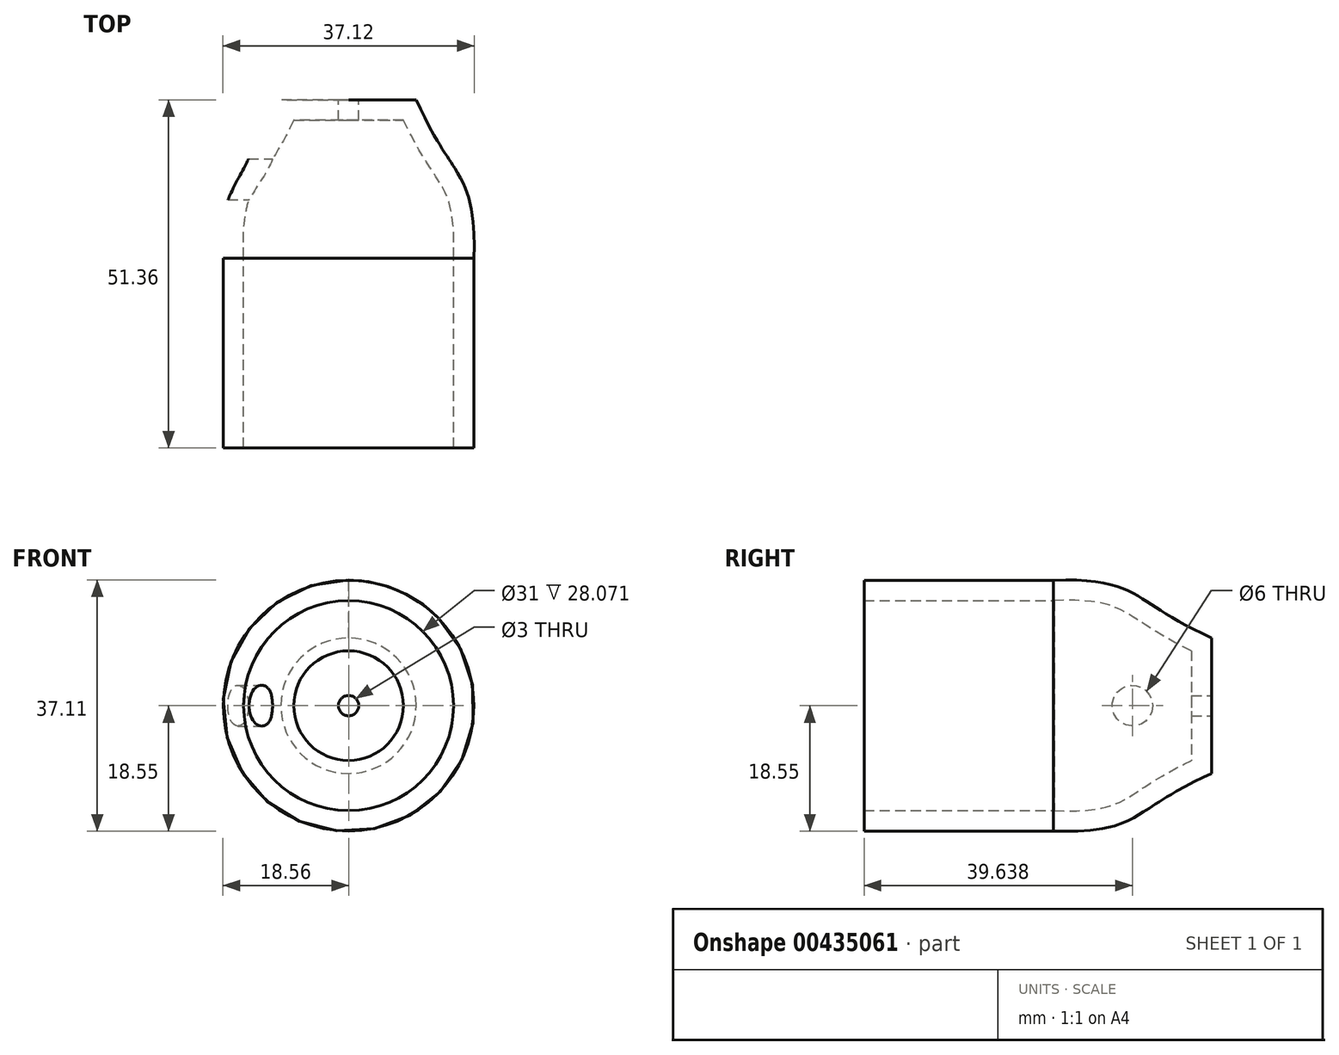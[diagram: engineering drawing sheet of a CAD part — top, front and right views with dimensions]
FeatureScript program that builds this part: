
annotation { "Feature Type Name" : "Feature", "Feature Type Description" : "" }
export const myFeature = defineFeature(function(context is Context, id is Id, definition is map)
    precondition{}
    {
        {
            var Q0;
            Q0=qCreatedBy(makeId("Front.planeOp"),FACE);
            var sketch = newSketch(context, id + "F0", { "sketchPlane" : qUnion([Q0])});
            skCircle(sketch, "E0", {"center": v(0, 0) * mm, "radius": 15.5 * mm});
            skCircle(sketch, "E1.0", {"center": v(0, 0) * mm, "radius": 18.5 * mm});
            skSolve(sketch);
        }
        {
            var Q0;
            Q0 = qSketchRegion(id + "F0", true);
            extrude(context, id + "F1", {"entities" : qUnion([Q0]), "depth" : 28 * mm});
        }
        {
            var Q0;
            Q0=qCreatedBy(makeId("Top.planeOp"),FACE);
            var sketch = newSketch(context, id + "F2", { "sketchPlane" : qUnion([Q0])});
            skLineSegment(sketch, "E2", {"start": v(0, 0) * mm, "end": v(-18.5, 0) * mm});
            skLineSegment(sketch, "E3", {"start": v(0, 23.36) * mm, "end": v(-10, 23.36) * mm});
            skFitSpline(sketch, "E4", {"points": [v(-10, 23.36) * mm, v(-15.86, 12.99) * mm, v(-18.5, 0) * mm], "startDerivative": vector(-16.01, -35.2) * mm, "endDerivative": vector(2.08, -43.63) * mm});
            skLineSegment(sketch, "E5", {"start": v(0, 23.36) * mm, "end": v(0, 0) * mm});
            skSolve(sketch);
        }
        {
            var Q0;
            Q0=makeQuery(id+"F2.imprint","IMPRINT",FACE,{"disambiguationData":[TD([[makeQuery(id+"F2.imprint","IMPRINT",EDGE,{"derivedFrom":sQuery(id+"F2.wireOp",EDGE,"E2")}),-1.0]])]});
            var Q1;
            Q1=sQuery(id+"F2.wireOp",EDGE,"E5");
            revolve(context, id + "F3", {"operationType" : NewBodyOperationType.ADD, "entities" : qUnion([Q0]), "axis" : qUnion([Q1]), "revolveType" : RevolveType.FULL});
        }
        {
            var Q0;
            Q0=makeQuery(id+"F3.opRevolve","SWEPT_FACE",FACE,{"disambiguationData":[OSD([sQuery(id+"F2.wireOp",EDGE,"E2")])]});
            shell(context, id + "F4", {"entities" : qUnion([Q0]), "thickness" : 3 * mm});
        }
        {
            var Q0;
            Q0=makeQuery(id+"F3.opRevolve","SWEPT_FACE",FACE,{"disambiguationData":[OSD([sQuery(id+"F2.wireOp",EDGE,"E3")])]});
            var sketch = newSketch(context, id + "F5", { "sketchPlane" : qUnion([Q0])});
            skCircle(sketch, "E6", {"center": v(0, 0) * mm, "radius": 1.5 * mm});
            skSolve(sketch);
        }
        {
            var Q0;
            Q0 = qSketchRegion(id + "F5", true);
            extrude(context, id + "F6", {"entities" : qUnion([Q0]), "operationType" : NewBodyOperationType.REMOVE, "oppositeDirection" : true, "depth" : 25 * mm});
        }
        {
            var Q0;
            Q0=qCreatedBy(makeId("Right.planeOp"),FACE);
            var sketch = newSketch(context, id + "F7", { "sketchPlane" : qUnion([Q0])});
            skCircle(sketch, "E7", {"center": v(11.64, 0) * mm, "radius": 3 * mm});
            skSolve(sketch);
        }
        {
            var Q0;
            Q0 = qSketchRegion(id + "F7", true);
            extrude(context, id + "F8", {"entities" : qUnion([Q0]), "operationType" : NewBodyOperationType.REMOVE, "oppositeDirection" : true, "depth" : 25 * mm});
        }
    });
